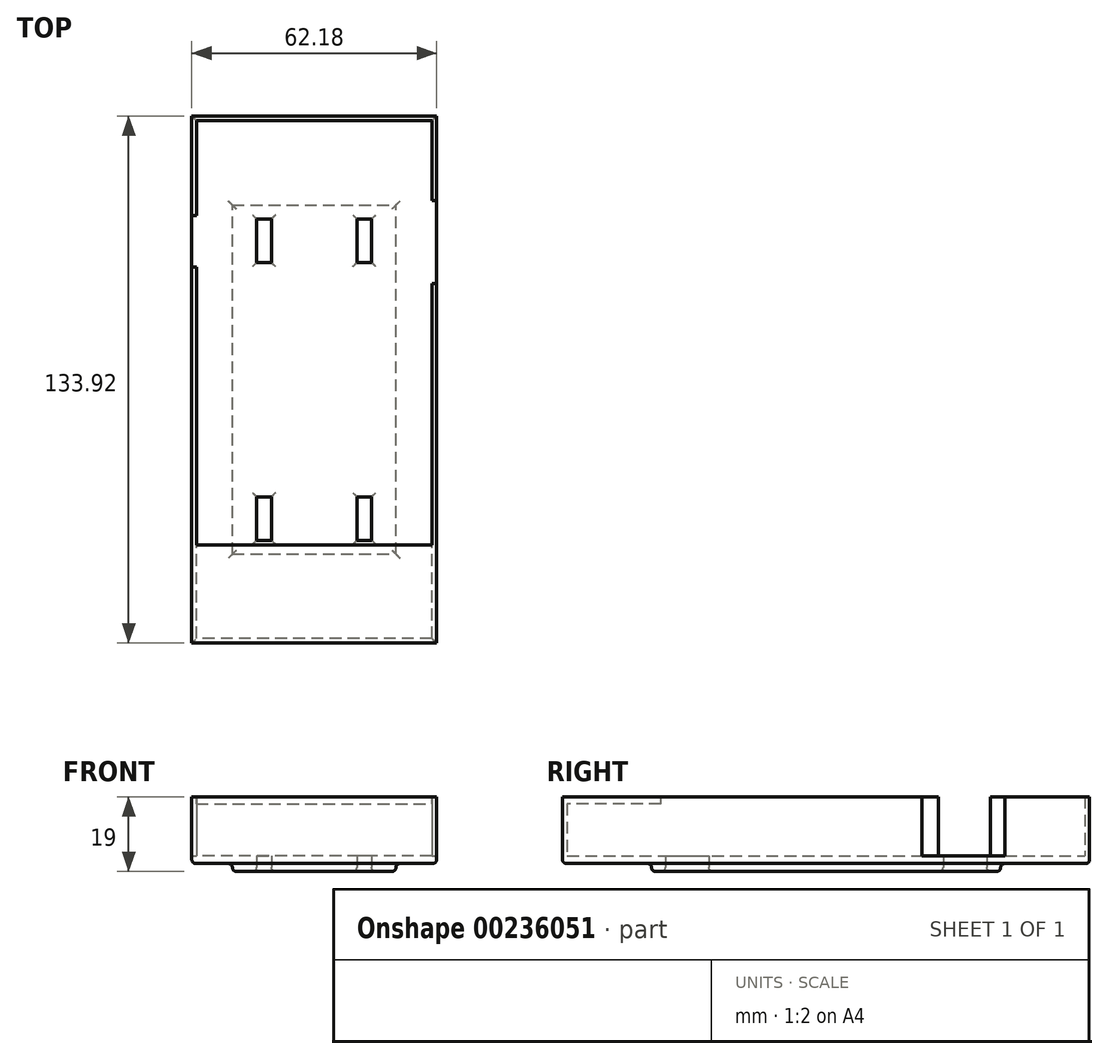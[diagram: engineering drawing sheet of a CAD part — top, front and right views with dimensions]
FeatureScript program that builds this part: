
annotation { "Feature Type Name" : "Feature", "Feature Type Description" : "" }
export const myFeature = defineFeature(function(context is Context, id is Id, definition is map)
    precondition{}
    {
        {
            var Q0;
            Q0=qCreatedBy(makeId("Top.planeOp"),FACE);
            var sketch = newSketch(context, id + "F0", { "sketchPlane" : qUnion([Q0])});
            skLineSegment(sketch, "E0.bottom", {"start": v(31.1, -66.96) * mm, "end": v(-31.1, -66.96) * mm});
            skLineSegment(sketch, "E0.top", {"start": v(31.1, 66.96) * mm, "end": v(-31.1, 66.96) * mm});
            skLineSegment(sketch, "E0.left", {"start": v(31.1, -66.96) * mm, "end": v(31.1, 66.96) * mm});
            skLineSegment(sketch, "E0.right", {"start": v(-31.1, -66.96) * mm, "end": v(-31.1, 66.96) * mm});
            skPoint(sketch, "E0.middle", {"position": v(0, 0) * mm});
            skSolve(sketch);
        }
        {
            var Q0;
            Q0 = qSketchRegion(id + "F0", true);
            extrude(context, id + "F1", {"entities" : qUnion([Q0]), "depth" : 2 * mm});
        }
        {
            var Q0;
            Q0=makeQuery(id+"F1.opExtrude","CAP_FACE",FACE,{"disambiguationData":[OSD([sQuery(id+"F0.wireOp",EDGE,"E0.bottom"),sQuery(id+"F0.wireOp",EDGE,"E0.top"),sQuery(id+"F0.wireOp",EDGE,"E0.left"),sQuery(id+"F0.wireOp",EDGE,"E0.right")])],"isStart":false});
            var sketch = newSketch(context, id + "F2", { "sketchPlane" : qUnion([Q0])});
            skLineSegment(sketch, "E1.bottom", {"start": v(31.1, -66.96) * mm, "end": v(-31.1, -66.96) * mm});
            skLineSegment(sketch, "E1.top", {"start": v(31.1, 66.96) * mm, "end": v(-31.1, 66.96) * mm});
            skLineSegment(sketch, "E1.left", {"start": v(31.1, -66.96) * mm, "end": v(31.1, 66.96) * mm});
            skLineSegment(sketch, "E1.right", {"start": v(-31.1, -66.96) * mm, "end": v(-31.1, 66.96) * mm});
            skPoint(sketch, "E1.middle", {"position": v(0, 0) * mm});
            skLineSegment(sketch, "E2.0", {"start": v(29.9, 65.76) * mm, "end": v(-29.9, 65.76) * mm});
            skLineSegment(sketch, "E2.1", {"start": v(29.9, -65.76) * mm, "end": v(29.9, 65.76) * mm});
            skLineSegment(sketch, "E2.2", {"start": v(29.9, -65.76) * mm, "end": v(-29.9, -65.76) * mm});
            skLineSegment(sketch, "E2.3", {"start": v(-29.9, -65.76) * mm, "end": v(-29.9, 65.76) * mm});
            skLineSegment(sketch, "E3.bottom", {"start": v(-31.1, 41.71) * mm, "end": v(-29.9, 41.71) * mm});
            skLineSegment(sketch, "E3.top", {"start": v(-31.1, 28.56) * mm, "end": v(-29.9, 28.56) * mm});
            skLineSegment(sketch, "E3.left", {"start": v(-31.1, 41.71) * mm, "end": v(-31.1, 28.56) * mm});
            skLineSegment(sketch, "E3.right", {"start": v(-29.9, 41.71) * mm, "end": v(-29.9, 28.56) * mm});
            skLineSegment(sketch, "E4.bottom", {"start": v(29.9, 45.44) * mm, "end": v(31.1, 45.44) * mm});
            skLineSegment(sketch, "E4.top", {"start": v(29.9, 24.37) * mm, "end": v(31.1, 24.37) * mm});
            skLineSegment(sketch, "E4.left", {"start": v(29.9, 45.44) * mm, "end": v(29.9, 24.37) * mm});
            skLineSegment(sketch, "E4.right", {"start": v(31.1, 45.44) * mm, "end": v(31.1, 24.37) * mm});
            skSolve(sketch);
        }
        {
            var Q0;
            {var subQ2=sQuery(id+"F2.wireOp",EDGE,"E1.top");Q0=makeQuery(id+"F2.imprint","IMPRINT",FACE,{"disambiguationData":[TD([[makeQuery(id+"F2.imprint","IMPRINT",EDGE,{"derivedFrom":subQ2}),1.0]])]});}
            var Q1;
            {var subQ4=sQuery(id+"F2.wireOp",EDGE,"E1.bottom");Q1=makeQuery(id+"F2.imprint","IMPRINT",FACE,{"disambiguationData":[TD([[makeQuery(id+"F2.imprint","IMPRINT",EDGE,{"derivedFrom":subQ4}),-1.0]])]});}
            extrude(context, id + "F3", {"entities" : qUnion([Q0, Q1]), "operationType" : NewBodyOperationType.ADD, "depth" : 15 * mm});
        }
        {
            var Q0;
            Q0=makeQuery(id+"F3.boolean.opBoolean","MERGE",FACE,{"derivedFrom":[makeQuery(id+"F1.opExtrude","SWEPT_FACE",FACE,{"disambiguationData":[OSD([sQuery(id+"F0.wireOp",EDGE,"E0.bottom")])]}),makeQuery(id+"F3.opExtrude","SWEPT_FACE",FACE,{"disambiguationData":[OSD([sQuery(id+"F2.wireOp",EDGE,"E1.bottom")])]})]});
            var sketch = newSketch(context, id + "F4", { "sketchPlane" : qUnion([Q0])});
            skLineSegment(sketch, "E5.bottom", {"start": v(-31.1, 17) * mm, "end": v(31.1, 17) * mm});
            skLineSegment(sketch, "E5.top", {"start": v(-31.1, 15.21) * mm, "end": v(31.1, 15.21) * mm});
            skLineSegment(sketch, "E5.left", {"start": v(-31.1, 17) * mm, "end": v(-31.1, 15.21) * mm});
            skLineSegment(sketch, "E5.right", {"start": v(31.1, 17) * mm, "end": v(31.1, 15.21) * mm});
            skSolve(sketch);
        }
        {
            var Q0;
            Q0 = qSketchRegion(id + "F4", true);
            extrude(context, id + "F5", {"entities" : qUnion([Q0]), "operationType" : NewBodyOperationType.ADD, "oppositeDirection" : true, "depth" : 25 * mm});
        }
        {
            var Q0;
            Q0=makeQuery(id+"F1.opExtrude","CAP_FACE",FACE,{"disambiguationData":[OSD([sQuery(id+"F0.wireOp",EDGE,"E0.bottom"),sQuery(id+"F0.wireOp",EDGE,"E0.top"),sQuery(id+"F0.wireOp",EDGE,"E0.left"),sQuery(id+"F0.wireOp",EDGE,"E0.right")])],"isStart":true});
            var sketch = newSketch(context, id + "F6", { "sketchPlane" : qUnion([Q0])});
            skLineSegment(sketch, "E6.bottom", {"start": v(-20.77, 44.35) * mm, "end": v(20.77, 44.35) * mm});
            skLineSegment(sketch, "E6.top", {"start": v(-20.77, -44.35) * mm, "end": v(20.77, -44.35) * mm});
            skLineSegment(sketch, "E6.left", {"start": v(-20.77, 44.35) * mm, "end": v(-20.77, -44.35) * mm});
            skLineSegment(sketch, "E6.right", {"start": v(20.77, 44.35) * mm, "end": v(20.77, -44.35) * mm});
            skPoint(sketch, "E6.middle", {"position": v(0, 0) * mm});
            skSolve(sketch);
        }
        {
            var Q0;
            Q0 = qSketchRegion(id + "F6", true);
            extrude(context, id + "F7", {"entities" : qUnion([Q0]), "operationType" : NewBodyOperationType.ADD, "depth" : 2 * mm});
        }
        {
            var Q0;
            Q0=makeQuery(id+"F7.opExtrude","CAP_FACE",FACE,{"disambiguationData":[OSD([sQuery(id+"F6.wireOp",EDGE,"E6.bottom"),sQuery(id+"F6.wireOp",EDGE,"E6.top"),sQuery(id+"F6.wireOp",EDGE,"E6.left"),sQuery(id+"F6.wireOp",EDGE,"E6.right")])],"isStart":false});
            var sketch = newSketch(context, id + "F8", { "sketchPlane" : qUnion([Q0])});
            skLineSegment(sketch, "E7.bottom", {"start": v(10.86, -29.76) * mm, "end": v(14.61, -29.76) * mm});
            skLineSegment(sketch, "E7.top", {"start": v(10.86, -40.82) * mm, "end": v(14.61, -40.82) * mm});
            skLineSegment(sketch, "E7.left", {"start": v(10.86, -29.76) * mm, "end": v(10.86, -40.82) * mm});
            skLineSegment(sketch, "E7.right", {"start": v(14.61, -29.76) * mm, "end": v(14.61, -40.82) * mm});
            skPoint(sketch, "E7.middle", {"position": v(12.74, -35.3) * mm});
            skLineSegment(sketch, "E8.bottom", {"start": v(13.45, 0) * mm, "end": v(-13.45, 0) * mm, "construction": true});
            skLineSegment(sketch, "E8.top", {"start": v(13.45, 0) * mm, "end": v(-13.45, 0) * mm, "construction": true});
            skLineSegment(sketch, "E8.left", {"start": v(13.45, 0) * mm, "end": v(13.45, 0) * mm});
            skLineSegment(sketch, "E8.right", {"start": v(-13.45, 0) * mm, "end": v(-13.45, 0) * mm});
            skPoint(sketch, "E8.middle", {"position": v(0, 0) * mm});
            skLineSegment(sketch, "E9.bottom", {"start": v(0, -16.43) * mm, "end": v(0, -16.43) * mm});
            skLineSegment(sketch, "E9.top", {"start": v(0, 16.43) * mm, "end": v(0, 16.43) * mm});
            skLineSegment(sketch, "E9.left", {"start": v(0, -16.43) * mm, "end": v(0, 16.43) * mm, "construction": true});
            skLineSegment(sketch, "E9.right", {"start": v(0, -16.43) * mm, "end": v(0, 16.43) * mm, "construction": true});
            skLineSegment(sketch, "E10.MirrorCS", {"start": v(-10.86, -29.76) * mm, "end": v(-10.86, -40.82) * mm});
            skLineSegment(sketch, "E11.MirrorCS", {"start": v(-10.86, -40.82) * mm, "end": v(-14.61, -40.82) * mm});
            skLineSegment(sketch, "E12.MirrorCS", {"start": v(-14.61, -29.76) * mm, "end": v(-14.61, -40.82) * mm});
            skLineSegment(sketch, "E13.MirrorCS", {"start": v(-10.86, -29.76) * mm, "end": v(-14.61, -29.76) * mm});
            skLineSegment(sketch, "E14.MirrorCS", {"start": v(-10.86, 29.76) * mm, "end": v(-10.86, 40.82) * mm});
            skLineSegment(sketch, "E15.MirrorCS", {"start": v(-10.86, 40.82) * mm, "end": v(-14.61, 40.82) * mm});
            skLineSegment(sketch, "E16.MirrorCS", {"start": v(-14.61, 29.76) * mm, "end": v(-14.61, 40.82) * mm});
            skPoint(sketch, "E17.MirrorP", {"position": v(12.74, 35.3) * mm});
            skLineSegment(sketch, "E18.MirrorCS", {"start": v(14.61, 29.76) * mm, "end": v(14.61, 40.82) * mm});
            skLineSegment(sketch, "E19.MirrorCS", {"start": v(-10.86, 29.76) * mm, "end": v(-14.61, 29.76) * mm});
            skLineSegment(sketch, "E20.MirrorCS", {"start": v(10.86, 29.76) * mm, "end": v(10.86, 40.82) * mm});
            skLineSegment(sketch, "E21.MirrorCS", {"start": v(10.86, 40.82) * mm, "end": v(14.61, 40.82) * mm});
            skLineSegment(sketch, "E22.MirrorCS", {"start": v(10.86, 29.76) * mm, "end": v(14.61, 29.76) * mm});
            skSolve(sketch);
        }
        {
            var Q0;
            Q0 = qSketchRegion(id + "F8", true);
            extrude(context, id + "F9", {"entities" : qUnion([Q0]), "operationType" : NewBodyOperationType.REMOVE, "oppositeDirection" : true, "depth" : 8 * mm});
        }
        {
            var Q0;
            Q0=makeQuery(id+"F7.opExtrude","CAP_FACE",FACE,{"disambiguationData":[OSD([sQuery(id+"F6.wireOp",EDGE,"E6.bottom"),sQuery(id+"F6.wireOp",EDGE,"E6.top"),sQuery(id+"F6.wireOp",EDGE,"E6.left"),sQuery(id+"F6.wireOp",EDGE,"E6.right")])],"isStart":false});
            var Q1;
            Q1=makeQuery(id+"F1.opExtrude","CAP_FACE",FACE,{"disambiguationData":[OSD([sQuery(id+"F0.wireOp",EDGE,"E0.bottom"),sQuery(id+"F0.wireOp",EDGE,"E0.top"),sQuery(id+"F0.wireOp",EDGE,"E0.left"),sQuery(id+"F0.wireOp",EDGE,"E0.right")])],"isStart":true});
            fillet(context, id + "F10", {"entities" : qUnion([Q0, Q1]), "radius" : 1 * mm, "tangentPropagation" : true, "allowEdgeOverflow" : false});
        }
    });
